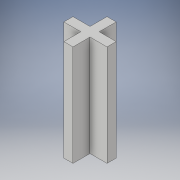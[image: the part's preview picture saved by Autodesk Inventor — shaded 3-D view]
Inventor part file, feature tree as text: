
AUTODESK INVENTOR PART (.ipt)
format: ipt  version: 2019 (Build 230136000, 136)  size: 101,376 bytes
history: native  units: mm
features: extrude x1, sketch x1
ambient origin geometry x8: Origin, YZ Plane, XZ Plane, XY Plane, X Axis, Y Axis, Z Axis, Center Point
bodies: Solid1 (feature_tree)
feature tree (2):
  extrude  "Extrusion1"  Depth=3.18mm
  sketch  "Sketch1"  dims[d0=15.0mm d1=3.18mm d2=3.18mm d3=15.0mm d4=35.0mm d5=0.0mm]
